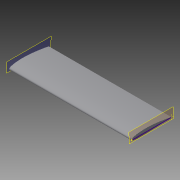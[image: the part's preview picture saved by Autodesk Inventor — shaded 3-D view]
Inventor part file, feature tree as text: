
AUTODESK INVENTOR PART (.ipt)
format: ipt  version: 2015 (Build 190159000, 159)  size: 89,600 bytes
history: native  units: in
note: dims shown in document units (in); Inventor stores cm internally (conversion verified against a paired STEP export)
features: other x3, plane x3, sketch x2
ambient origin geometry x8: Origin, YZ Plane, XZ Plane, XY Plane, X Axis, Y Axis, Z Axis, Center Point
bodies: Solid1 (feature_tree)
feature tree (8):
  other  "Generic Wing 1.ipt"
  other  "Solid1::Generic Wing 1.ipt"
  other  "TaggingFeature1"
  sketch  "Sketch1"  dims[d0=0.3937in]
  sketch  "Sketch2"
  plane  "Work Plane1"
  plane  "Work Plane2"
  plane  "Work Plane3"
